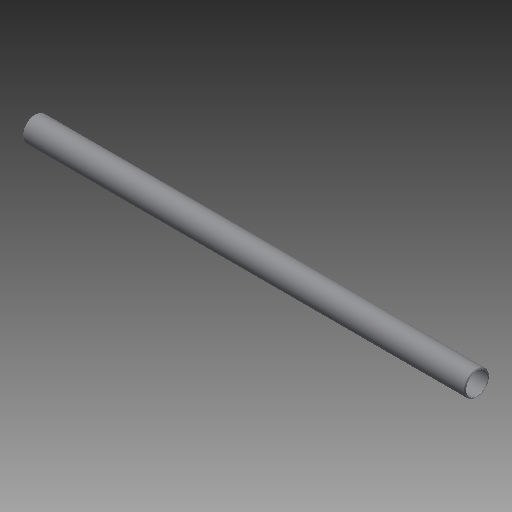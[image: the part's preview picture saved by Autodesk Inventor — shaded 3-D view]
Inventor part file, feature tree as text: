
AUTODESK INVENTOR PART (.ipt)
format: ipt  version: 2019 (Build 230136000, 136)  size: 128,512 bytes
history: native  units: in
note: dims shown in document units (in); Inventor stores cm internally (conversion verified against a paired STEP export)
features: other x42, revolve x1, sketch x1
ambient origin geometry x8: Origin, YZ Plane, XZ Plane, XY Plane, X Axis, Y Axis, Z Axis, Center Point
bodies: Solid1 (feature_tree)
feature tree (44):
  revolve  "Revolution1"  [1 undecoded]
  other  "cp1_XY"
  other  "cp1_YZ"
  other  "cp1_ZX"
  other  "cp1_X"
  other  "cp1_Y"
  other  "cp1_Z"
  other  "cp1_Center"
  other  "cp2_XY"
  other  "cp2_YZ"
  other  "cp2_ZX"
  other  "cp2_X"
  other  "cp2_Y"
  other  "cp2_Z"
  other  "cp2_Center"
  other  "cp3_XY"
  other  "cp3_YZ"
  other  "cp3_ZX"
  other  "cp3_X"
  other  "cp3_Y"
  other  "cp3_Z"
  other  "cp3_Center"
  other  "cp4_XY"
  other  "cp4_YZ"
  other  "cp4_ZX"
  other  "cp4_X"
  other  "cp4_Y"
  other  "cp4_Z"
  other  "cp4_Center"
  other  "tube_front_XY"
  other  "tube_front_YZ"
  other  "tube_front_ZX"
  other  "tube_front_X"
  other  "tube_front_Y"
  other  "tube_front_Z"
  other  "tube_front_Center"
  other  "tube_rear_XY"
  other  "tube_rear_YZ"
  other  "tube_rear_ZX"
  other  "tube_rear_X"
  other  "tube_rear_Y"
  other  "tube_rear_Z"
  other  "tube_rear_Center"
  sketch  "Sketch_1"  dims[d0=360.0deg]
note: 1 required parameter value undecoded (feature->parameter linkage not recoverable at this tier; creation-order binding heuristic only, values carry confidence <= 0.55)
